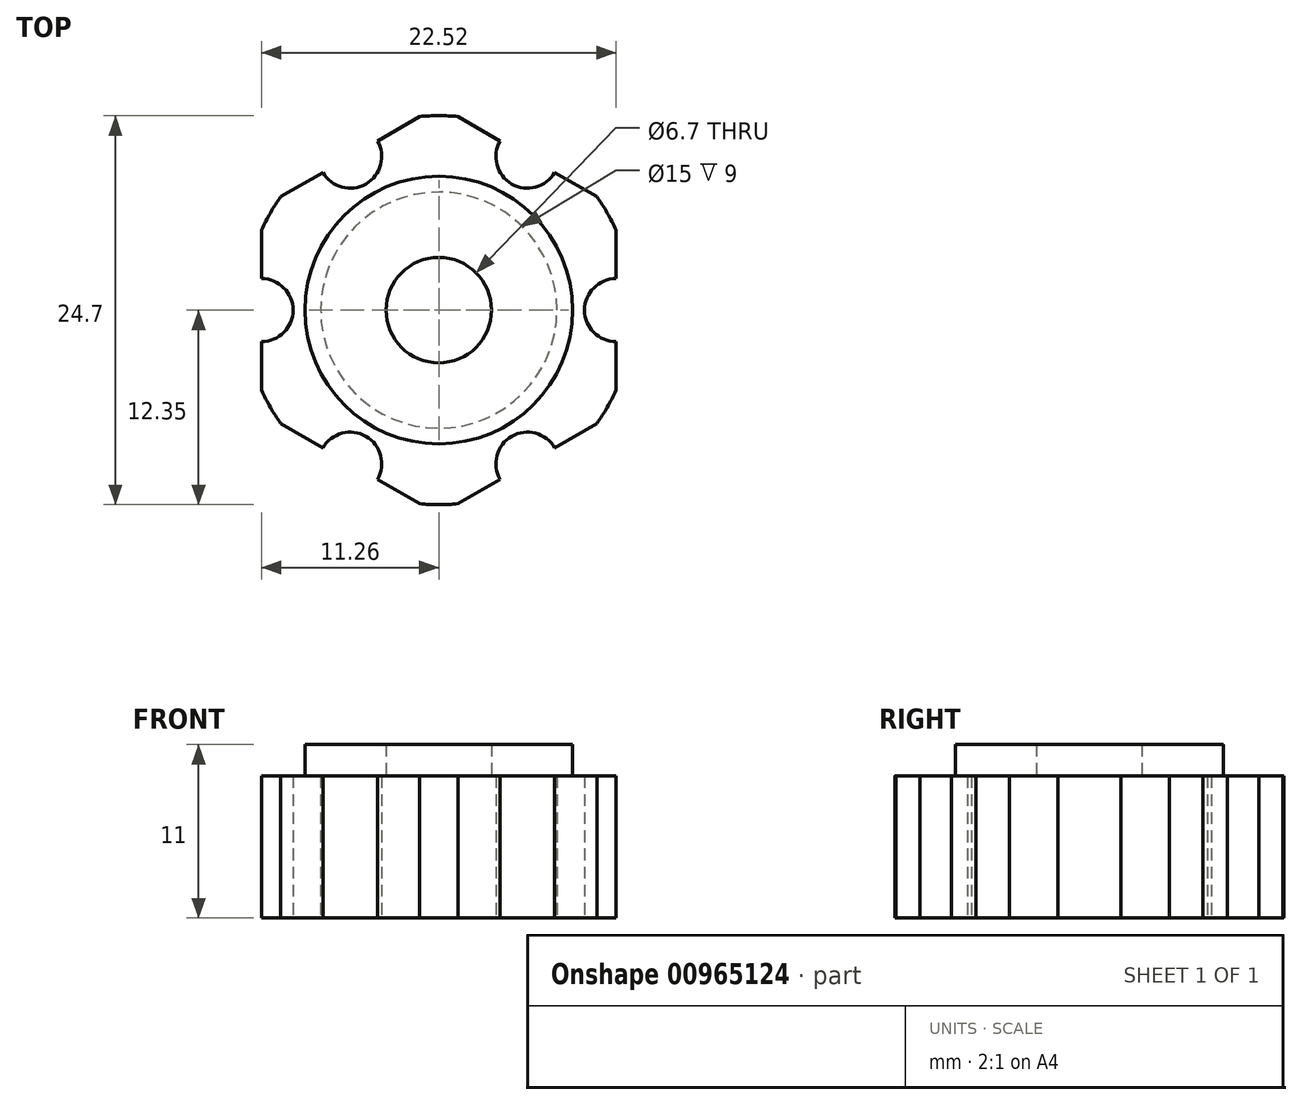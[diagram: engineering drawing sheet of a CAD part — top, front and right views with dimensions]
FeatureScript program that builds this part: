
annotation { "Feature Type Name" : "Feature", "Feature Type Description" : "" }
export const myFeature = defineFeature(function(context is Context, id is Id, definition is map)
    precondition{}
    {
        {
            var Q0;
            Q0=qCreatedBy(makeId("Top.planeOp"),FACE);
            var sketch = newSketch(context, id + "F0", { "sketchPlane" : qUnion([Q0])});
            skCircle(sketch, "E0.cCircle", {"center": v(0, 0) * mm, "radius": 11.26 * mm, "construction": true});
            skLineSegment(sketch, "E0.0", {"start": v(-11.26, -6.5) * mm, "end": v(-11.26, 6.5) * mm});
            skLineSegment(sketch, "E0.1", {"start": v(-11.26, 6.5) * mm, "end": v(0, 13) * mm});
            skLineSegment(sketch, "E0.2", {"start": v(0, 13) * mm, "end": v(11.26, 6.5) * mm});
            skLineSegment(sketch, "E0.3", {"start": v(11.26, 6.5) * mm, "end": v(11.26, -6.5) * mm});
            skLineSegment(sketch, "E0.4", {"start": v(11.26, -6.5) * mm, "end": v(0, -13) * mm});
            skLineSegment(sketch, "E0.5", {"start": v(0, -13) * mm, "end": v(-11.26, -6.5) * mm});
            skPoint(sketch, "E0.0.midPoint", {"position": v(-11.26, 0) * mm});
            skCircle(sketch, "E1", {"center": v(0, 0) * mm, "radius": 8.5 * mm});
            skCircle(sketch, "E2", {"center": v(0, 0) * mm, "radius": 3.35 * mm});
            skCircle(sketch, "E3", {"center": v(-5.63, 9.75) * mm, "radius": 2 * mm});
            skCircle(sketch, "E4", {"center": v(5.63, 9.75) * mm, "radius": 2 * mm});
            skCircle(sketch, "E5", {"center": v(11.26, 0) * mm, "radius": 2 * mm});
            skCircle(sketch, "E6", {"center": v(-5.63, -9.75) * mm, "radius": 2 * mm});
            skCircle(sketch, "E7", {"center": v(-11.26, 0) * mm, "radius": 2 * mm});
            skCircle(sketch, "E8", {"center": v(5.63, -9.75) * mm, "radius": 2 * mm});
            skCircle(sketch, "E9", {"center": v(0, 0) * mm, "radius": 12.35 * mm});
            skSolve(sketch);
        }
        {
            var Q0;
            Q0=makeQuery(id+"F0.imprint","IMPRINT",FACE,{"disambiguationData":[TD([[makeQuery(id+"F0.imprint","IMPRINT",EDGE,{"derivedFrom":sQuery(id+"F0.wireOp",EDGE,"E1")}),-1.0]])]});
            extrude(context, id + "F1", {"entities" : qUnion([Q0]), "depth" : 9 * mm, "offsetDistance" : 25 * mm});
        }
        {
            var Q0;
            Q0=makeQuery(id+"F0.imprint","IMPRINT",FACE,{"disambiguationData":[TD([[makeQuery(id+"F0.imprint","IMPRINT",EDGE,{"derivedFrom":sQuery(id+"F0.wireOp",EDGE,"E1")}),1.0]])]});
            extrude(context, id + "F2", {"entities" : qUnion([Q0]), "operationType" : NewBodyOperationType.ADD, "depth" : 11 * mm, "offsetDistance" : 25 * mm});
        }
        {
            var Q0;
            {var subQ0=sQuery(id+"F0.wireOp",EDGE,"E1");Q0=makeQuery(id+"F2.boolean.opBoolean","MERGE",FACE,{"derivedFrom":[makeQuery(id+"F1.opExtrude","CAP_FACE",FACE,{"disambiguationData":[OSD([sQuery(id+"F0.wireOp",EDGE,"E0.0"),sQuery(id+"F0.wireOp",EDGE,"E0.1"),sQuery(id+"F0.wireOp",EDGE,"E0.2"),sQuery(id+"F0.wireOp",EDGE,"E0.3"),sQuery(id+"F0.wireOp",EDGE,"E0.4"),sQuery(id+"F0.wireOp",EDGE,"E0.5"),subQ0,sQuery(id+"F0.wireOp",EDGE,"E3"),sQuery(id+"F0.wireOp",EDGE,"E4"),sQuery(id+"F0.wireOp",EDGE,"E5"),sQuery(id+"F0.wireOp",EDGE,"E6"),sQuery(id+"F0.wireOp",EDGE,"E7"),sQuery(id+"F0.wireOp",EDGE,"E8")])],"isStart":true}),makeQuery(id+"F2.opExtrude","CAP_FACE",FACE,{"disambiguationData":[OSD([subQ0,sQuery(id+"F0.wireOp",EDGE,"E2")])],"isStart":true})]});}
            var sketch = newSketch(context, id + "F3", { "sketchPlane" : qUnion([Q0])});
            skCircle(sketch, "E10", {"center": v(0, 0) * mm, "radius": 7.5 * mm});
            skCircle(sketch, "E11", {"center": v(0, 0) * mm, "radius": 2 * mm});
            skSolve(sketch);
        }
        {
            var Q0;
            Q0=makeQuery(id+"F3.imprint","IMPRINT",FACE,{"disambiguationData":[TD([[makeQuery(id+"F3.imprint","IMPRINT",EDGE,{"derivedFrom":sQuery(id+"F3.wireOp",EDGE,"E10")}),1.0]])]});
            extrude(context, id + "F4", {"entities" : qUnion([Q0]), "operationType" : NewBodyOperationType.REMOVE, "oppositeDirection" : true, "depth" : 9 * mm, "offsetDistance" : 25 * mm});
        }
    });
